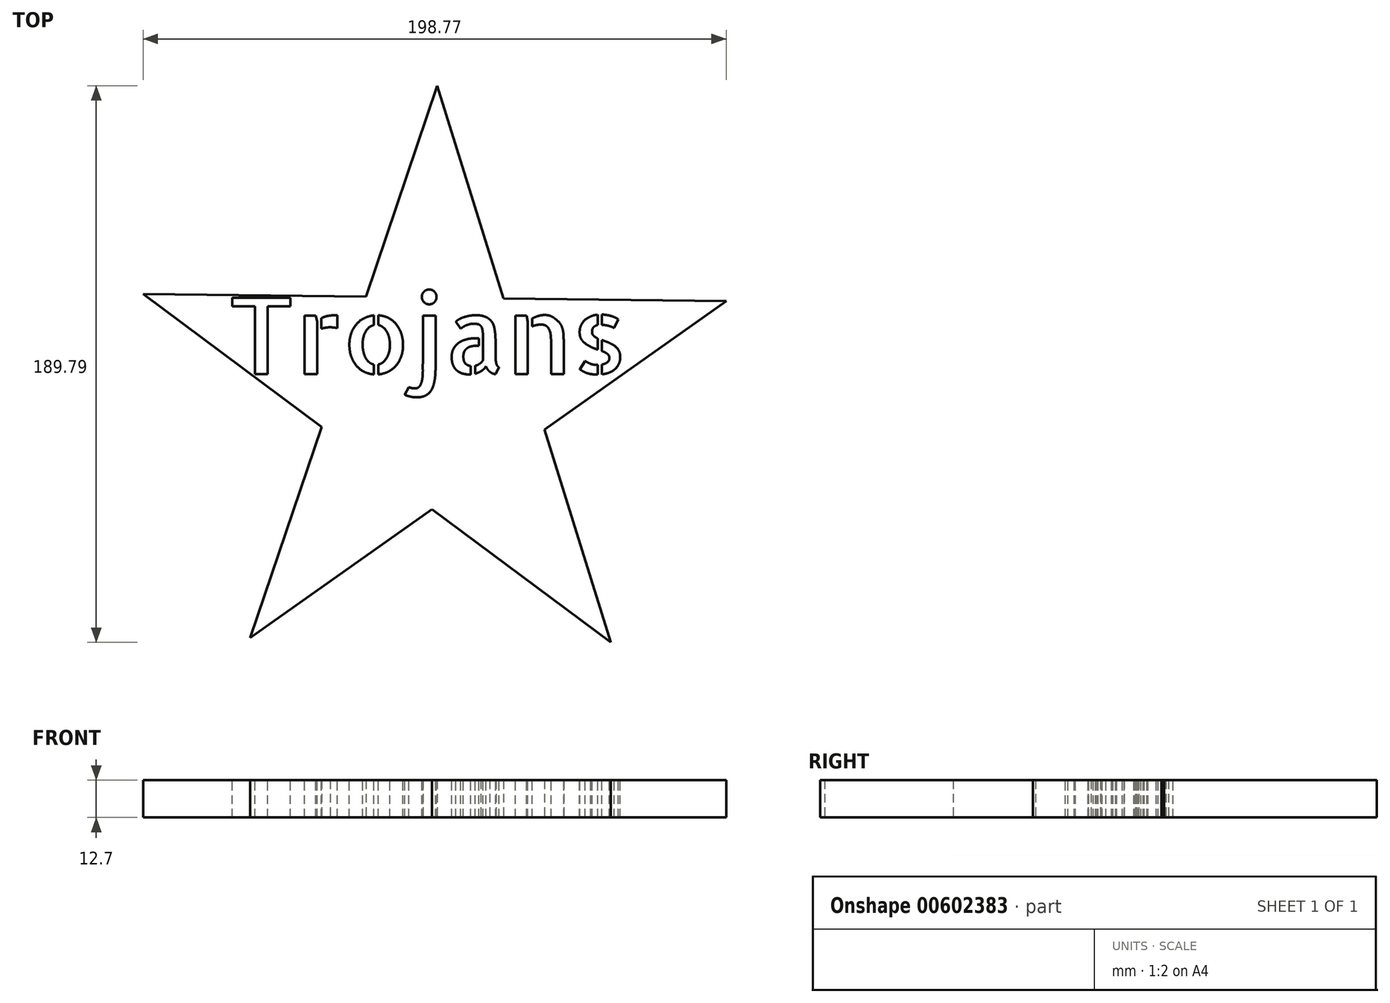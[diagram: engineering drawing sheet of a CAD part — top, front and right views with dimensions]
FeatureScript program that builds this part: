
annotation { "Feature Type Name" : "Feature", "Feature Type Description" : "" }
export const myFeature = defineFeature(function(context is Context, id is Id, definition is map)
    precondition{}
    {
        {
            var Q0;
            Q0=qCreatedBy(makeId("Top.planeOp"),FACE);
            var sketch = newSketch(context, id + "F0", { "sketchPlane" : qUnion([Q0])});
            skCircle(sketch, "E0.cCircle", {"center": v(0, 0) * mm, "radius": 32.3 * mm, "construction": true});
            skLineSegment(sketch, "E0.0", {"start": v(-23.07, 32.58) * mm, "end": v(23.86, 32) * mm});
            skLineSegment(sketch, "E0.1", {"start": v(23.86, 32) * mm, "end": v(37.81, -12.8) * mm});
            skLineSegment(sketch, "E0.2", {"start": v(37.81, -12.8) * mm, "end": v(-0.49, -39.91) * mm});
            skLineSegment(sketch, "E0.3", {"start": v(-0.49, -39.91) * mm, "end": v(-38.11, -11.87) * mm});
            skLineSegment(sketch, "E0.4", {"start": v(-38.11, -11.87) * mm, "end": v(-23.07, 32.58) * mm});
            skPoint(sketch, "E0.0.midPoint", {"position": v(0.4, 32.3) * mm});
            skLineSegment(sketch, "E1.1", {"start": v(37.81, -12.8) * mm, "end": v(23.86, 32) * mm});
            skLineSegment(sketch, "E2.1", {"start": v(-0.49, -39.91) * mm, "end": v(37.81, -12.8) * mm});
            skLineSegment(sketch, "E3", {"start": v(23.86, 32) * mm, "end": v(99.78, 31.07) * mm});
            skLineSegment(sketch, "E4", {"start": v(99.78, 31.07) * mm, "end": v(37.81, -12.8) * mm});
            skLineSegment(sketch, "E5", {"start": v(-0.49, -39.91) * mm, "end": v(-62.46, -83.79) * mm});
            skLineSegment(sketch, "E6", {"start": v(-62.46, -83.79) * mm, "end": v(-38.11, -11.87) * mm});
            skLineSegment(sketch, "E7", {"start": v(-38.11, -11.87) * mm, "end": v(-98.99, 33.5) * mm});
            skLineSegment(sketch, "E8", {"start": v(-98.99, 33.5) * mm, "end": v(-23.07, 32.58) * mm});
            skLineSegment(sketch, "E9", {"start": v(-23.07, 32.58) * mm, "end": v(1.28, 104.5) * mm});
            skLineSegment(sketch, "E10", {"start": v(1.28, 104.5) * mm, "end": v(23.86, 32) * mm});
            skLineSegment(sketch, "E11", {"start": v(37.81, -12.8) * mm, "end": v(60.39, -85.3) * mm});
            skLineSegment(sketch, "E12", {"start": v(-0.49, -39.91) * mm, "end": v(60.39, -85.3) * mm});
            skSolve(sketch);
        }
        {
            var Q0;
            Q0 = qSketchRegion(id + "F0", true);
            extrude(context, id + "F1", {"entities" : qUnion([Q0]), "depth" : 12.7 * mm, "offsetDistance" : 25.4 * mm});
        }
        {
            var Q0;
            Q0=qCreatedBy(makeId("Top.planeOp"),FACE);
            var sketch = newSketch(context, id + "F2", { "sketchPlane" : qUnion([Q0])});
            skText(sketch, "E13", { "text": "Trojans", "fontName": "AllertaStencil-Regular.ttf"});
            const initialGuessF2  = {"E13": [-0.07037, 0.00623, 1, 0, 0.02602]};
            skSetInitialGuess(sketch, initialGuessF2);
            skSolve(sketch);
        }
        {
            var Q0;
            Q0 = qSketchRegion(id + "F2", true);
            extrude(context, id + "F3", {"entities" : qUnion([Q0]), "operationType" : NewBodyOperationType.REMOVE, "oppositeDirection" : true, "depth" : 25.4 * mm, "offsetDistance" : 25.4 * mm, "hasSecondDirection" : true, "secondDirectionOppositeDirection" : false, "secondDirectionDepth" : 25.4 * mm});
        }
    });
